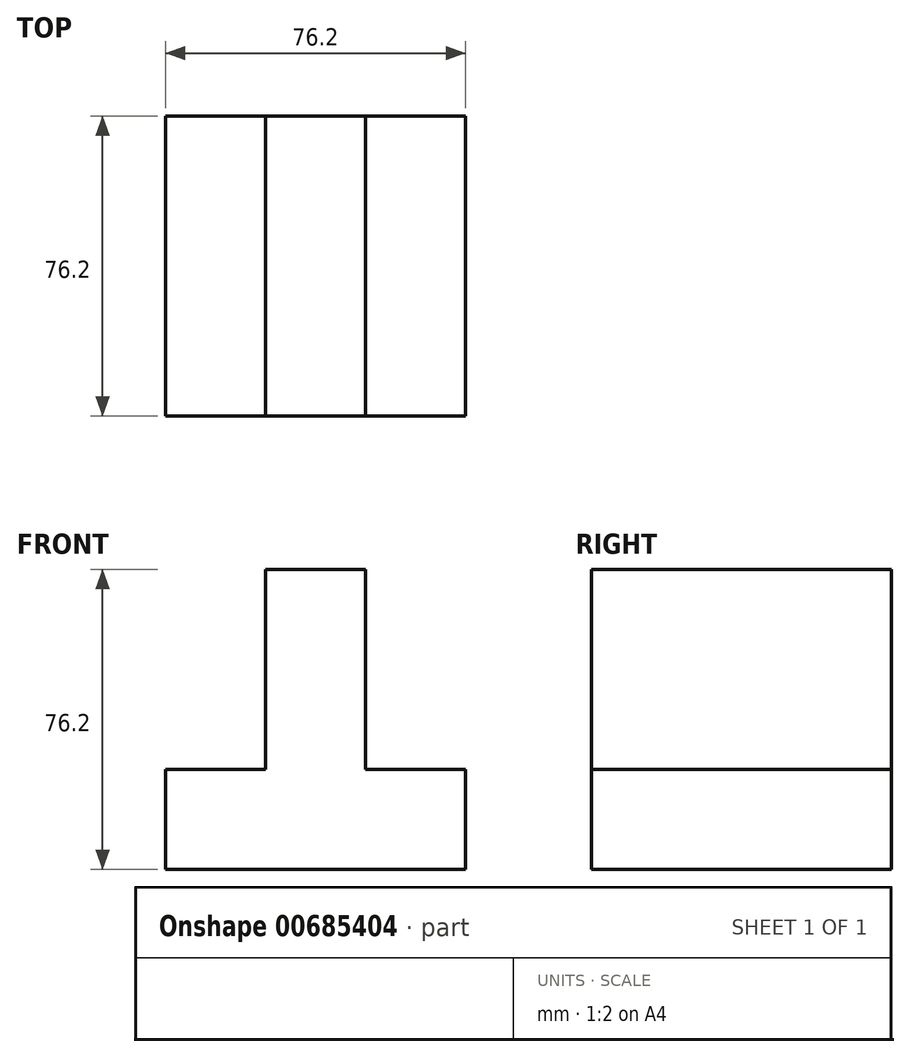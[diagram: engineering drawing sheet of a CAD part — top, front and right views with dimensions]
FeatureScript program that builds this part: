
annotation { "Feature Type Name" : "Feature", "Feature Type Description" : "" }
export const myFeature = defineFeature(function(context is Context, id is Id, definition is map)
    precondition{}
    {
        {
            var Q0;
            Q0=qCreatedBy(makeId("Front.planeOp"),FACE);
            var sketch = newSketch(context, id + "F0", { "sketchPlane" : qUnion([Q0])});
            skLineSegment(sketch, "E0", {"start": v(0, 0) * mm, "end": v(-76.2, 0) * mm});
            skLineSegment(sketch, "E1", {"start": v(-76.2, 0) * mm, "end": v(-76.17, 76.2) * mm});
            skLineSegment(sketch, "E2", {"start": v(-76.17, 76.2) * mm, "end": v(0, 76.2) * mm});
            skLineSegment(sketch, "E3", {"start": v(0, 76.2) * mm, "end": v(0, 0) * mm});
            skSolve(sketch);
        }
        {
            var Q0;
            Q0=makeQuery(id+"F0.imprint","IMPRINT",FACE,{"disambiguationData":[TD([[makeQuery(id+"F0.imprint","IMPRINT",EDGE,{"derivedFrom":sQuery(id+"F0.wireOp",EDGE,"E0")}),-1.0]])]});
            extrude(context, id + "F1", {"entities" : qUnion([Q0]), "depth" : 76.2 * mm, "offsetDistance" : 25.4 * mm});
        }
        {
            var Q0;
            Q0=makeQuery(id+"F1.opExtrude","CAP_FACE",FACE,{"disambiguationData":[OSD([sQuery(id+"F0.wireOp",EDGE,"E0"),sQuery(id+"F0.wireOp",EDGE,"E1"),sQuery(id+"F0.wireOp",EDGE,"E2"),sQuery(id+"F0.wireOp",EDGE,"E3")])],"isStart":false});
            var sketch = newSketch(context, id + "F2", { "sketchPlane" : qUnion([Q0])});
            skLineSegment(sketch, "E4", {"start": v(-76.2, 0) * mm, "end": v(-76.2, 25.4) * mm});
            skLineSegment(sketch, "E5", {"start": v(-76.2, 25.4) * mm, "end": v(-50.8, 25.4) * mm});
            skLineSegment(sketch, "E6", {"start": v(-50.8, 25.4) * mm, "end": v(-50.8, 76.2) * mm});
            skLineSegment(sketch, "E7", {"start": v(-50.8, 76.2) * mm, "end": v(-25.4, 76.2) * mm});
            skLineSegment(sketch, "E8", {"start": v(-25.4, 76.2) * mm, "end": v(-25.4, 25.4) * mm});
            skLineSegment(sketch, "E9", {"start": v(-25.4, 25.4) * mm, "end": v(0, 25.4) * mm});
            skSolve(sketch);
        }
        {
            var Q0;
            {var subQ0=sQuery(id+"F2.wireOp",EDGE,"E5");Q0=makeQuery(id+"F2.imprint","IMPRINT",FACE,{"disambiguationData":[TD([[makeQuery(id+"F2.imprint","IMPRINT",EDGE,{"derivedFrom":subQ0}),1.0]])]});}
            extrude(context, id + "F3", {"entities" : qUnion([Q0]), "operationType" : NewBodyOperationType.REMOVE, "oppositeDirection" : true, "depth" : 76.2 * mm, "offsetDistance" : 25.4 * mm});
        }
        {
            var Q0;
            Q0=makeQuery(id+"F1.opExtrude","CAP_FACE",FACE,{"disambiguationData":[OSD([sQuery(id+"F0.wireOp",EDGE,"E0"),sQuery(id+"F0.wireOp",EDGE,"E1"),sQuery(id+"F0.wireOp",EDGE,"E2"),sQuery(id+"F0.wireOp",EDGE,"E3")])],"isStart":false});
            var sketch = newSketch(context, id + "F4", { "sketchPlane" : qUnion([Q0])});
            skLineSegment(sketch, "E10", {"start": v(0, 0) * mm, "end": v(0, 25.4) * mm});
            skLineSegment(sketch, "E11", {"start": v(0, 25.4) * mm, "end": v(-25.4, 25.4) * mm});
            skLineSegment(sketch, "E12", {"start": v(-25.4, 25.4) * mm, "end": v(-25.4, 76.2) * mm});
            skSolve(sketch);
        }
        {
            var Q0;
            {var subQ0=sQuery(id+"F4.wireOp",EDGE,"E11");Q0=makeQuery(id+"F4.imprint","IMPRINT",FACE,{"disambiguationData":[TD([[makeQuery(id+"F4.imprint","IMPRINT",EDGE,{"derivedFrom":subQ0}),-1.0]])]});}
            extrude(context, id + "F5", {"entities" : qUnion([Q0]), "operationType" : NewBodyOperationType.REMOVE, "oppositeDirection" : true, "depth" : 76.2 * mm, "offsetDistance" : 25.4 * mm});
        }
    });
